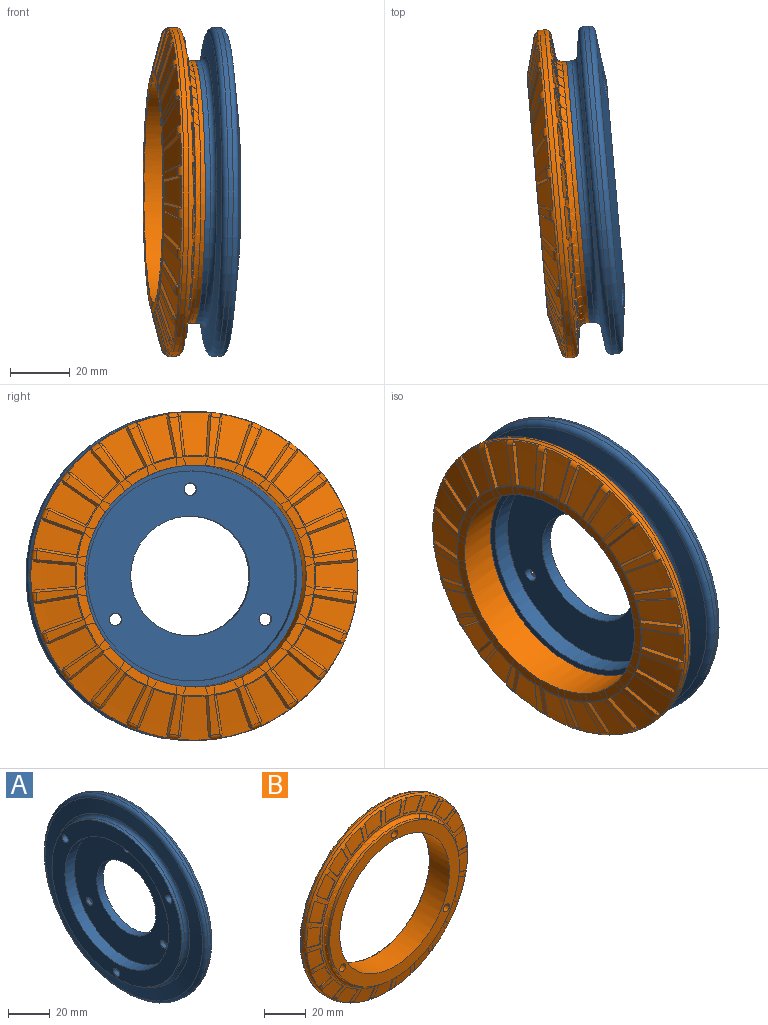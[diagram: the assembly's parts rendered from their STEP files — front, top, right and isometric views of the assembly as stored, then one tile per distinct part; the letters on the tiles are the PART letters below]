
ASSEMBLY  parts=2 mates=1
PART A: 28 faces, bbox 12.7x119.1x119.1 mm
  f0: cone r=53.26mm half-angle=82.5deg, axis (-1,0,0), area 4769.5mm2, adj f1,f12,f21,f24,f27
  f1: torus R=53mm, axis (-1,0,0), area 983.9mm2, adj f0,f2
  f2: cylinder r=55mm len=110mm, axis (-1,0,0), area 573.7mm2, adj f1,f3
  f3: torus R=53mm, axis (-1,0,0), area 983.9mm2, adj f2,f4
  f4: cone r=45.61mm half-angle=82.5deg, axis (1,0,0), area 2395.9mm2, adj f3,f5
  f5: torus R=45.88mm, axis (-1,0,0), area 805.2mm2, adj f4,f6
  f6: cylinder r=43.88mm len=87.75mm, axis (-1,0,0), area 481.3mm2, adj f5,f7
  f7: plane 87.75x87.75mm, normal (-1,0,0), area 2130.1mm2, adj f6,f8,f19,f22,f25
  f8: cylinder r=35.12mm len=70.25mm, axis (-1,0,0), area 1423.4mm2, adj f7,f9
  f9: plane 70.25x70.25mm, normal (-1,0,0), area 2577.8mm2, adj f8,f10,f13,f15,f17
  f10: cylinder r=20mm len=40mm, axis (-1,0,0), area 534.1mm2, adj f9,f11
  f11: plane 71x71mm, normal (1,0,0), area 2551.8mm2, adj f10,f12,f14,f16,f18
  f12: cylinder r=35.5mm len=71mm, axis (-1,0,0), area 446.1mm2, adj f0,f11
  f13: cylinder r=2.1mm len=4.2mm, axis (1,0,0), area 31mm2, adj f9,f14
  f14: cone r=2.1mm half-angle=45deg, axis (1,0,0), area 51.5mm2, adj f11,f13
  f15: cylinder r=2.1mm len=4.2mm, axis (1,0,0), area 31mm2, adj f9,f16
  f16: cone r=2.1mm half-angle=45deg, axis (1,0,0), area 51.5mm2, adj f11,f15
  f17: cylinder r=2.1mm len=4.2mm, axis (1,0,0), area 31mm2, adj f9,f18
  f18: cone r=2.1mm half-angle=45deg, axis (1,0,0), area 51.5mm2, adj f11,f17
  f19: cylinder r=2.1mm len=7.7mm, axis (1,0,0), area 101.6mm2, adj f7,f20
  f20: plane 9.75x9.75mm, normal (1,0,0), area 60.8mm2, adj f19,f21
  f21: cylinder r=4.88mm len=9.75mm, axis (1,0,0), area 132.4mm2, adj f0,f20
  f22: cylinder r=2.1mm len=7.7mm, axis (1,0,0), area 101.6mm2, adj f7,f23
  f23: plane 9.75x9.75mm, normal (1,0,0), area 60.8mm2, adj f22,f24
  f24: cylinder r=4.88mm len=9.75mm, axis (1,0,0), area 132.4mm2, adj f0,f23
  f25: cylinder r=2.1mm len=7.7mm, axis (1,0,0), area 101.6mm2, adj f7,f26
  f26: plane 9.75x9.75mm, normal (1,0,0), area 60.8mm2, adj f25,f27
  f27: cylinder r=4.88mm len=9.75mm, axis (1,0,0), area 132.4mm2, adj f0,f26
PART B: 328 faces, bbox 119.2x14.6x119.2 mm
  f0: revolved ~12.32x11.5mm, area 83mm2, adj f1,f2,f3,f92
  f1: plane 7.92x1.5mm, normal (-0.99,0,-0.16), area 2.9mm2, adj f0,f2,f92,f93
  f2: revolved ~93.19x93.17mm, area 112.1mm2, adj f0,f1,f3,f93
  f3: plane 7.5x2.93mm, normal (0.93,0,0.36), area 2.9mm2, adj f0,f2,f92,f93
  f4: revolved ~13.82x11.86mm, area 83mm2, adj f5,f6,f7,f92
  f5: plane 7.34x3.32mm, normal (-0.91,0,-0.41), area 2.9mm2, adj f4,f6,f92,f93
  f6: revolved ~93.18x93.17mm, area 112.1mm2, adj f4,f5,f7,f93
  f7: plane 6.51x4.75mm, normal (0.81,0,0.59), area 2.9mm2, adj f4,f6,f92,f93
  f8: revolved ~14.37x11.42mm, area 83mm2, adj f9,f10,f11,f92
  f9: plane 6.25x5.08mm, normal (-0.78,0,-0.63), area 2.9mm2, adj f8,f10,f92,f93
  f10: revolved ~8.25x5.29mm, area 3.6mm2, adj f8,f9,f11,f93
  f11: plane 6.25x5.08mm, normal (0.63,0,0.78), area 2.9mm2, adj f8,f10,f92,f93
  f12: revolved ~13.95x10.19mm, area 83mm2, adj f13,f14,f15,f92
  f13: plane 6.51x4.75mm, normal (-0.59,0,-0.81), area 2.9mm2, adj f12,f14,f92,f93
  f14: revolved ~9.32x2.99mm, area 3.6mm2, adj f12,f13,f15,f93
  f15: plane 7.34x3.32mm, normal (0.41,0,0.91), area 2.9mm2, adj f12,f14,f92,f93
  f16: revolved ~12.58x8.3mm, area 83mm2, adj f17,f18,f19,f92
  f17: plane 7.5x2.93mm, normal (-0.36,0,-0.93), area 2.9mm2, adj f16,f18,f92,f93
  f18: revolved ~93.21x93.1mm, area 112.1mm2, adj f16,f17,f19,f93
  f19: plane 7.92x1.5mm, normal (0.16,0,0.99), area 2.9mm2, adj f16,f18,f92,f93
  f20: revolved ~11.18x9.98mm, area 83mm2, adj f21,f22,f23,f92
  f21: plane 7.98x1.5mm, normal (-0.1,0,-0.99), area 2.9mm2, adj f20,f22,f92,f93
  f22: revolved ~9.53x2.14mm, area 3.6mm2, adj f20,f21,f23,f93
  f23: plane 7.98x1.5mm, normal (-0.1,0,0.99), area 2.9mm2, adj f20,f22,f92,f93
  f24: revolved ~12.32x11.5mm, area 83mm2, adj f25,f26,f27,f92
  f25: plane 7.92x1.5mm, normal (0.16,0,-0.99), area 2.9mm2, adj f24,f26,f92,f93
  f26: revolved ~93.19x93.17mm, area 112.1mm2, adj f24,f25,f27,f93
  f27: plane 7.5x2.93mm, normal (-0.36,0,0.93), area 2.9mm2, adj f24,f26,f92,f93
  f28: revolved ~13.82x11.86mm, area 83mm2, adj f29,f30,f31,f92
  f29: plane 7.34x3.32mm, normal (0.41,0,-0.91), area 2.9mm2, adj f28,f30,f92,f93
  f30: revolved ~93.18x93.17mm, area 112.1mm2, adj f28,f29,f31,f93
  f31: plane 6.51x4.75mm, normal (-0.59,0,0.81), area 2.9mm2, adj f28,f30,f92,f93
  f32: revolved ~14.37x11.42mm, area 83mm2, adj f33,f34,f35,f92
  f33: plane 6.25x5.08mm, normal (0.63,0,-0.78), area 2.9mm2, adj f32,f34,f92,f93
  f34: revolved ~8.25x5.29mm, area 3.6mm2, adj f32,f33,f35,f93
  f35: plane 6.25x5.08mm, normal (-0.78,0,0.63), area 2.9mm2, adj f32,f34,f92,f93
  f36: revolved ~13.95x10.19mm, area 83mm2, adj f37,f38,f39,f92
  f37: plane 6.51x4.75mm, normal (0.81,0,-0.59), area 2.9mm2, adj f36,f38,f92,f93
  f38: revolved ~9.32x2.99mm, area 3.6mm2, adj f36,f37,f39,f93
  f39: plane 7.34x3.32mm, normal (-0.91,0,0.41), area 2.9mm2, adj f36,f38,f92,f93
  f40: revolved ~12.58x8.3mm, area 83mm2, adj f41,f42,f43,f92
  f41: plane 7.5x2.93mm, normal (0.93,0,-0.36), area 2.9mm2, adj f40,f42,f92,f93
  f42: revolved ~93.21x93.1mm, area 112.1mm2, adj f40,f41,f43,f93
  f43: plane 7.92x1.5mm, normal (-0.99,0,0.16), area 2.9mm2, adj f40,f42,f92,f93
  f44: revolved ~11.18x9.98mm, area 83mm2, adj f45,f46,f47,f92
  f45: plane 7.98x1.5mm, normal (0.99,0,-0.1), area 2.9mm2, adj f44,f46,f92,f93
  f46: revolved ~9.53x2.14mm, area 3.6mm2, adj f44,f45,f47,f93
  f47: plane 7.98x1.5mm, normal (-0.99,0,-0.1), area 2.9mm2, adj f44,f46,f92,f93
  f48: revolved ~12.32x11.5mm, area 83mm2, adj f49,f50,f51,f92
  f49: plane 7.92x1.5mm, normal (0.99,0,0.16), area 2.9mm2, adj f48,f50,f92,f93
  f50: revolved ~93.19x93.17mm, area 112.1mm2, adj f48,f49,f51,f93
  f51: plane 7.5x2.93mm, normal (-0.93,0,-0.36), area 2.9mm2, adj f48,f50,f92,f93
  f52: revolved ~13.82x11.86mm, area 83mm2, adj f53,f54,f55,f92
  f53: plane 7.34x3.32mm, normal (0.91,0,0.41), area 2.9mm2, adj f52,f54,f92,f93
  f54: revolved ~93.18x93.17mm, area 112.1mm2, adj f52,f53,f55,f93
  f55: plane 6.51x4.75mm, normal (-0.81,0,-0.59), area 2.9mm2, adj f52,f54,f92,f93
  f56: revolved ~14.37x11.42mm, area 83mm2, adj f57,f58,f59,f92
  f57: plane 6.25x5.08mm, normal (0.78,0,0.63), area 2.9mm2, adj f56,f58,f92,f93
  f58: revolved ~8.25x5.29mm, area 3.6mm2, adj f56,f57,f59,f93
  f59: plane 6.25x5.08mm, normal (-0.63,0,-0.78), area 2.9mm2, adj f56,f58,f92,f93
  f60: revolved ~13.95x10.19mm, area 83mm2, adj f61,f62,f63,f92
  f61: plane 6.51x4.75mm, normal (0.59,0,0.81), area 2.9mm2, adj f60,f62,f92,f93
  f62: revolved ~9.32x2.99mm, area 3.6mm2, adj f60,f61,f63,f93
  f63: plane 7.34x3.32mm, normal (-0.41,0,-0.91), area 2.9mm2, adj f60,f62,f92,f93
  f64: revolved ~12.58x8.3mm, area 83mm2, adj f65,f66,f67,f92
  f65: plane 7.5x2.93mm, normal (0.36,0,0.93), area 2.9mm2, adj f64,f66,f92,f93
  f66: revolved ~93.21x93.1mm, area 112.1mm2, adj f64,f65,f67,f93
  f67: plane 7.92x1.5mm, normal (-0.16,0,-0.99), area 2.9mm2, adj f64,f66,f92,f93
  f68: revolved ~11.18x9.98mm, area 83mm2, adj f69,f70,f71,f92
  f69: plane 7.98x1.5mm, normal (0.1,0,0.99), area 2.9mm2, adj f68,f70,f92,f93
  f70: revolved ~9.53x2.14mm, area 3.6mm2, adj f68,f69,f71,f93
  f71: plane 7.98x1.5mm, normal (0.1,0,-0.99), area 2.9mm2, adj f68,f70,f92,f93
  f72: revolved ~12.32x11.5mm, area 83mm2, adj f73,f74,f75,f92
  f73: plane 7.92x1.5mm, normal (-0.16,0,0.99), area 2.9mm2, adj f72,f74,f92,f93
  f74: revolved ~93.19x93.17mm, area 112.1mm2, adj f72,f73,f75,f93
  f75: plane 7.5x2.93mm, normal (0.36,0,-0.93), area 2.9mm2, adj f72,f74,f92,f93
  f76: revolved ~13.82x11.86mm, area 83mm2, adj f77,f78,f79,f92
  f77: plane 7.34x3.32mm, normal (-0.41,0,0.91), area 2.9mm2, adj f76,f78,f92,f93
  f78: revolved ~93.18x93.17mm, area 112.1mm2, adj f76,f77,f79,f93
  f79: plane 6.51x4.75mm, normal (0.59,0,-0.81), area 2.9mm2, adj f76,f78,f92,f93
  f80: revolved ~14.37x11.42mm, area 83mm2, adj f81,f82,f83,f92
  f81: plane 6.25x5.08mm, normal (-0.63,0,0.78), area 2.9mm2, adj f80,f82,f92,f93
  f82: revolved ~8.25x5.29mm, area 3.6mm2, adj f80,f81,f83,f93
  f83: plane 6.25x5.08mm, normal (0.78,0,-0.63), area 2.9mm2, adj f80,f82,f92,f93
  f84: revolved ~13.95x10.19mm, area 83mm2, adj f85,f86,f87,f92
  f85: plane 6.51x4.75mm, normal (-0.81,0,0.59), area 2.9mm2, adj f84,f86,f92,f93
  f86: revolved ~9.32x2.99mm, area 3.6mm2, adj f84,f85,f87,f93
  f87: plane 7.34x3.32mm, normal (0.91,0,-0.41), area 2.9mm2, adj f84,f86,f92,f93
  f88: revolved ~12.58x8.3mm, area 83mm2, adj f89,f90,f91,f92
  f89: plane 7.5x2.93mm, normal (-0.93,0,0.36), area 2.9mm2, adj f88,f90,f92,f93
  f90: revolved ~93.21x93.1mm, area 112.1mm2, adj f88,f89,f91,f93
  f91: plane 7.92x1.5mm, normal (0.99,0,-0.16), area 2.9mm2, adj f88,f90,f92,f93
  f92: torus R=53mm, axis (0,-1,0), area 639.7mm2, adj f0,f1,f3,f4,f5,f7,f8,f9
  f93: cone r=45.61mm half-angle=82.5deg, axis (0,1,0), area 724.2mm2, adj f1,f2,f3,f5,f6,f7,f9,f10
  f94: bspline ~15.1x6.29mm, area 17.1mm2, adj f95,f98,f99,f100,f101,f307
  f95: bspline ~1.52x1.3mm, area 0.9mm2, adj f94,f99,f308
  f96: bspline ~16.08x5.05mm, area 17.1mm2, adj f97,f98,f99,f101,f102,f307
  f97: bspline ~1.69x1.52mm, area 0.9mm2, adj f96,f99,f308
  f98: cone r=56.02mm half-angle=89.5deg, axis (0,1,0), area 0.3mm2, adj f94,f96,f101,f307
  f99: cone r=56.07mm half-angle=75.5deg, axis (0,-1,0), area 148.4mm2, adj f94,f95,f96,f97,f100,f102,f305,f308
  f100: plane 13.71x4.99mm, normal (0.94,0,0.34), area 0.9mm2, adj f94,f99,f101,f305
  f101: plane 8.33x5.04mm, normal (0,-1,0), area 24.7mm2, adj f94,f96,f98,f100,f102,f305
  f102: plane 14.37x3.85mm, normal (-0.98,0,-0.17), area 0.9mm2, adj f96,f99,f101,f305
  f103: bspline ~13.38x9.94mm, area 17.1mm2, adj f104,f107,f108,f109,f110,f307
  f104: bspline ~1.56x1.52mm, area 0.9mm2, adj f103,f108,f308
  f105: bspline ~15.01x7.4mm, area 17.1mm2, adj f106,f107,f108,f110,f111,f307
  f106: bspline ~1.76x1.52mm, area 0.9mm2, adj f105,f108,f308
  f107: cone r=56.02mm half-angle=89.5deg, axis (0,1,0), area 0.3mm2, adj f103,f105,f110,f307
  f108: cone r=56.07mm half-angle=75.5deg, axis (0,-1,0), area 148.4mm2, adj f103,f104,f105,f106,f109,f111,f305,f308
  f109: plane 11.95x8.37mm, normal (0.82,0,0.57), area 0.9mm2, adj f103,f108,f110,f305
  f110: plane 8.13x6.54mm, normal (0,-1,0), area 24.7mm2, adj f103,f105,f107,f109,f111,f305
  f111: plane 13.23x6.17mm, normal (-0.91,0,-0.42), area 0.9mm2, adj f105,f108,f110,f305
  f112: bspline ~12.92x10.76mm, area 17.1mm2, adj f113,f116,f117,f118,f119,f307
  f113: bspline ~1.72x1.52mm, area 0.9mm2, adj f112,f117,f308
  f114: bspline ~12.92x10.76mm, area 17.1mm2, adj f115,f116,f117,f119,f120,f307
  f115: bspline ~1.72x1.52mm, area 0.9mm2, adj f114,f117,f308
  f116: cone r=56.02mm half-angle=89.5deg, axis (0,1,0), area 0.3mm2, adj f112,f114,f119,f307
  f117: cone r=56.07mm half-angle=75.5deg, axis (0,-1,0), area 148.4mm2, adj f112,f113,f114,f115,f118,f120,f305,f308
  f118: plane 11.18x9.38mm, normal (0.64,0,0.77), area 0.9mm2, adj f112,f117,f119,f305
  f119: plane 7.6x7.6mm, normal (0,-1,0), area 24.7mm2, adj f112,f114,f116,f118,f120,f305
  f120: plane 11.18x9.38mm, normal (-0.77,0,-0.64), area 0.9mm2, adj f114,f117,f119,f305
  f121: bspline ~15.01x7.4mm, area 17.1mm2, adj f122,f125,f126,f127,f128,f307
  f122: bspline ~1.76x1.52mm, area 0.9mm2, adj f121,f126,f308
  f123: bspline ~13.38x9.94mm, area 17.1mm2, adj f124,f125,f126,f128,f129,f307
  f124: bspline ~1.56x1.52mm, area 0.9mm2, adj f123,f126,f308
  f125: cone r=56.02mm half-angle=89.5deg, axis (0,1,0), area 0.3mm2, adj f121,f123,f128,f307
  f126: cone r=56.07mm half-angle=75.5deg, axis (0,-1,0), area 148.4mm2, adj f121,f122,f123,f124,f127,f129,f305,f308
  f127: plane 13.23x6.17mm, normal (0.42,0,0.91), area 0.9mm2, adj f121,f126,f128,f305
  f128: plane 8.13x6.54mm, normal (0,-1,0), area 24.7mm2, adj f121,f123,f125,f127,f129,f305
  f129: plane 11.95x8.37mm, normal (-0.57,0,-0.82), area 0.9mm2, adj f123,f126,f128,f305
  f130: bspline ~16.08x5.05mm, area 17.1mm2, adj f131,f134,f135,f136,f137,f307
  f131: bspline ~1.69x1.52mm, area 0.9mm2, adj f130,f135,f308
  f132: bspline ~15.1x6.29mm, area 17.1mm2, adj f133,f134,f135,f137,f138,f307
  f133: bspline ~1.52x1.3mm, area 0.9mm2, adj f132,f135,f308
  f134: cone r=56.02mm half-angle=89.5deg, axis (0,1,0), area 0.3mm2, adj f130,f132,f137,f307
  f135: cone r=56.07mm half-angle=75.5deg, axis (0,-1,0), area 148.4mm2, adj f130,f131,f132,f133,f136,f138,f305,f308
  f136: plane 14.37x3.85mm, normal (0.17,0,0.98), area 0.9mm2, adj f130,f135,f137,f305
  f137: plane 8.33x5.04mm, normal (0,-1,0), area 24.7mm2, adj f130,f132,f134,f136,f138,f305
  f138: plane 13.71x4.99mm, normal (-0.34,0,-0.94), area 0.9mm2, adj f132,f135,f137,f305
  f139: bspline ~16.85x5.27mm, area 17.1mm2, adj f140,f143,f144,f145,f146,f307
  f140: bspline ~1.52x1.49mm, area 0.9mm2, adj f139,f144,f308
  f141: bspline ~16.85x5.27mm, area 17.1mm2, adj f142,f143,f144,f146,f147,f307
  f142: bspline ~1.52x1.49mm, area 0.9mm2, adj f141,f144,f308
  f143: cone r=56.02mm half-angle=89.5deg, axis (0,1,0), area 0.3mm2, adj f139,f141,f146,f307
  f144: cone r=56.07mm half-angle=75.5deg, axis (0,-1,0), area 148.4mm2, adj f139,f140,f141,f142,f145,f147,f305,f308
  f145: plane 14.54x3.85mm, normal (-0.09,0,1), area 0.9mm2, adj f139,f144,f146,f305
  f146: plane 8.62x3.43mm, normal (0,-1,0), area 24.7mm2, adj f139,f141,f143,f145,f147,f305
  f147: plane 14.54x3.85mm, normal (-0.09,0,-1), area 0.9mm2, adj f141,f144,f146,f305
  f148: bspline ~15.1x6.29mm, area 17.1mm2, adj f149,f152,f153,f154,f155,f307
  f149: bspline ~1.52x1.3mm, area 0.9mm2, adj f148,f153,f308
  f150: bspline ~16.08x5.05mm, area 17.1mm2, adj f151,f152,f153,f155,f156,f307
  f151: bspline ~1.69x1.52mm, area 0.9mm2, adj f150,f153,f308
  f152: cone r=56.02mm half-angle=89.5deg, axis (0,1,0), area 0.3mm2, adj f148,f150,f155,f307
  f153: cone r=56.07mm half-angle=75.5deg, axis (0,-1,0), area 148.4mm2, adj f148,f149,f150,f151,f154,f156,f305,f308
  f154: plane 13.71x4.99mm, normal (-0.34,0,0.94), area 0.9mm2, adj f148,f153,f155,f305
  f155: plane 8.33x5.04mm, normal (0,-1,0), area 24.7mm2, adj f148,f150,f152,f154,f156,f305
  f156: plane 14.37x3.85mm, normal (0.17,0,-0.98), area 0.9mm2, adj f150,f153,f155,f305
  f157: bspline ~13.38x9.94mm, area 17.1mm2, adj f158,f161,f162,f163,f164,f307
  f158: bspline ~1.56x1.52mm, area 0.9mm2, adj f157,f162,f308
  f159: bspline ~15.01x7.4mm, area 17.1mm2, adj f160,f161,f162,f164,f165,f307
  f160: bspline ~1.76x1.52mm, area 0.9mm2, adj f159,f162,f308
  f161: cone r=56.02mm half-angle=89.5deg, axis (0,1,0), area 0.3mm2, adj f157,f159,f164,f307
  f162: cone r=56.07mm half-angle=75.5deg, axis (0,-1,0), area 148.4mm2, adj f157,f158,f159,f160,f163,f165,f305,f308
  f163: plane 11.95x8.37mm, normal (-0.57,0,0.82), area 0.9mm2, adj f157,f162,f164,f305
  f164: plane 8.13x6.54mm, normal (0,-1,0), area 24.7mm2, adj f157,f159,f161,f163,f165,f305
  f165: plane 13.23x6.17mm, normal (0.42,0,-0.91), area 0.9mm2, adj f159,f162,f164,f305
  f166: bspline ~12.92x10.76mm, area 17.1mm2, adj f167,f170,f171,f172,f173,f307
  f167: bspline ~1.72x1.52mm, area 0.9mm2, adj f166,f171,f308
  f168: bspline ~12.92x10.76mm, area 17.1mm2, adj f169,f170,f171,f173,f174,f307
  f169: bspline ~1.72x1.52mm, area 0.9mm2, adj f168,f171,f308
  f170: cone r=56.02mm half-angle=89.5deg, axis (0,1,0), area 0.3mm2, adj f166,f168,f173,f307
  f171: cone r=56.07mm half-angle=75.5deg, axis (0,-1,0), area 148.4mm2, adj f166,f167,f168,f169,f172,f174,f305,f308
  f172: plane 11.18x9.38mm, normal (-0.77,0,0.64), area 0.9mm2, adj f166,f171,f173,f305
  f173: plane 7.6x7.6mm, normal (0,-1,0), area 24.7mm2, adj f166,f168,f170,f172,f174,f305
  f174: plane 11.18x9.38mm, normal (0.64,0,-0.77), area 0.9mm2, adj f168,f171,f173,f305
  f175: bspline ~15.01x7.4mm, area 17.1mm2, adj f176,f179,f180,f181,f182,f307
  f176: bspline ~1.76x1.52mm, area 0.9mm2, adj f175,f180,f308
  f177: bspline ~13.38x9.94mm, area 17.1mm2, adj f178,f179,f180,f182,f183,f307
  f178: bspline ~1.56x1.52mm, area 0.9mm2, adj f177,f180,f308
  f179: cone r=56.02mm half-angle=89.5deg, axis (0,1,0), area 0.3mm2, adj f175,f177,f182,f307
  f180: cone r=56.07mm half-angle=75.5deg, axis (0,-1,0), area 148.4mm2, adj f175,f176,f177,f178,f181,f183,f305,f308
  f181: plane 13.23x6.17mm, normal (-0.91,0,0.42), area 0.9mm2, adj f175,f180,f182,f305
  f182: plane 8.13x6.54mm, normal (0,-1,0), area 24.7mm2, adj f175,f177,f179,f181,f183,f305
  f183: plane 11.95x8.37mm, normal (0.82,0,-0.57), area 0.9mm2, adj f177,f180,f182,f305
  f184: bspline ~16.08x5.05mm, area 17.1mm2, adj f185,f188,f189,f190,f191,f307
  f185: bspline ~1.69x1.52mm, area 0.9mm2, adj f184,f189,f308
  f186: bspline ~15.1x6.29mm, area 17.1mm2, adj f187,f188,f189,f191,f192,f307
  f187: bspline ~1.52x1.3mm, area 0.9mm2, adj f186,f189,f308
  f188: cone r=56.02mm half-angle=89.5deg, axis (0,1,0), area 0.3mm2, adj f184,f186,f191,f307
  f189: cone r=56.07mm half-angle=75.5deg, axis (0,-1,0), area 148.4mm2, adj f184,f185,f186,f187,f190,f192,f305,f308
  f190: plane 14.37x3.85mm, normal (-0.98,0,0.17), area 0.9mm2, adj f184,f189,f191,f305
  f191: plane 8.33x5.04mm, normal (0,-1,0), area 24.7mm2, adj f184,f186,f188,f190,f192,f305
  f192: plane 13.71x4.99mm, normal (0.94,0,-0.34), area 0.9mm2, adj f186,f189,f191,f305
  f193: bspline ~16.85x5.27mm, area 17.1mm2, adj f194,f197,f198,f199,f200,f307
  f194: bspline ~1.52x1.49mm, area 0.9mm2, adj f193,f198,f308
  f195: bspline ~16.85x5.27mm, area 17.1mm2, adj f196,f197,f198,f200,f201,f307
  f196: bspline ~1.52x1.49mm, area 0.9mm2, adj f195,f198,f308
  f197: cone r=56.02mm half-angle=89.5deg, axis (0,1,0), area 0.3mm2, adj f193,f195,f200,f307
  f198: cone r=56.07mm half-angle=75.5deg, axis (0,-1,0), area 148.4mm2, adj f193,f194,f195,f196,f199,f201,f305,f308
  f199: plane 14.54x3.85mm, normal (-1,0,-0.09), area 0.9mm2, adj f193,f198,f200,f305
  f200: plane 8.62x3.43mm, normal (0,-1,0), area 24.7mm2, adj f193,f195,f197,f199,f201,f305
  f201: plane 14.54x3.85mm, normal (1,0,-0.09), area 0.9mm2, adj f195,f198,f200,f305
  f202: bspline ~15.1x6.29mm, area 17.1mm2, adj f203,f206,f207,f208,f209,f307
  f203: bspline ~1.52x1.3mm, area 0.9mm2, adj f202,f207,f308
  f204: bspline ~16.08x5.05mm, area 17.1mm2, adj f205,f206,f207,f209,f210,f307
  f205: bspline ~1.69x1.52mm, area 0.9mm2, adj f204,f207,f308
  f206: cone r=56.02mm half-angle=89.5deg, axis (0,1,0), area 0.3mm2, adj f202,f204,f209,f307
  f207: cone r=56.07mm half-angle=75.5deg, axis (0,-1,0), area 148.4mm2, adj f202,f203,f204,f205,f208,f210,f305,f308
  f208: plane 13.71x4.99mm, normal (-0.94,0,-0.34), area 0.9mm2, adj f202,f207,f209,f305
  f209: plane 8.33x5.04mm, normal (0,-1,0), area 24.7mm2, adj f202,f204,f206,f208,f210,f305
  f210: plane 14.37x3.85mm, normal (0.98,0,0.17), area 0.9mm2, adj f204,f207,f209,f305
  f211: bspline ~13.38x9.94mm, area 17.1mm2, adj f212,f215,f216,f217,f218,f307
  f212: bspline ~1.56x1.52mm, area 0.9mm2, adj f211,f216,f308
  f213: bspline ~15.01x7.4mm, area 17.1mm2, adj f214,f215,f216,f218,f219,f307
  f214: bspline ~1.76x1.52mm, area 0.9mm2, adj f213,f216,f308
  f215: cone r=56.02mm half-angle=89.5deg, axis (0,1,0), area 0.3mm2, adj f211,f213,f218,f307
  f216: cone r=56.07mm half-angle=75.5deg, axis (0,-1,0), area 148.4mm2, adj f211,f212,f213,f214,f217,f219,f305,f308
  f217: plane 11.95x8.37mm, normal (-0.82,0,-0.57), area 0.9mm2, adj f211,f216,f218,f305
  f218: plane 8.13x6.54mm, normal (0,-1,0), area 24.7mm2, adj f211,f213,f215,f217,f219,f305
  f219: plane 13.23x6.17mm, normal (0.91,0,0.42), area 0.9mm2, adj f213,f216,f218,f305
  f220: bspline ~12.92x10.76mm, area 17.1mm2, adj f221,f224,f225,f226,f227,f307
  f221: bspline ~1.72x1.52mm, area 0.9mm2, adj f220,f225,f308
  f222: bspline ~12.92x10.76mm, area 17.1mm2, adj f223,f224,f225,f227,f228,f307
  f223: bspline ~1.72x1.52mm, area 0.9mm2, adj f222,f225,f308
  f224: cone r=56.02mm half-angle=89.5deg, axis (0,1,0), area 0.3mm2, adj f220,f222,f227,f307
  f225: cone r=56.07mm half-angle=75.5deg, axis (0,-1,0), area 148.4mm2, adj f220,f221,f222,f223,f226,f228,f305,f308
  f226: plane 11.18x9.38mm, normal (-0.64,0,-0.77), area 0.9mm2, adj f220,f225,f227,f305
  f227: plane 7.6x7.6mm, normal (0,-1,0), area 24.7mm2, adj f220,f222,f224,f226,f228,f305
  f228: plane 11.18x9.38mm, normal (0.77,0,0.64), area 0.9mm2, adj f222,f225,f227,f305
  f229: bspline ~15.01x7.4mm, area 17.1mm2, adj f230,f233,f234,f235,f236,f307
  f230: bspline ~1.76x1.52mm, area 0.9mm2, adj f229,f234,f308
  f231: bspline ~13.38x9.94mm, area 17.1mm2, adj f232,f233,f234,f236,f237,f307
  f232: bspline ~1.56x1.52mm, area 0.9mm2, adj f231,f234,f308
  f233: cone r=56.02mm half-angle=89.5deg, axis (0,1,0), area 0.3mm2, adj f229,f231,f236,f307
  f234: cone r=56.07mm half-angle=75.5deg, axis (0,-1,0), area 148.4mm2, adj f229,f230,f231,f232,f235,f237,f305,f308
  f235: plane 13.23x6.17mm, normal (-0.42,0,-0.91), area 0.9mm2, adj f229,f234,f236,f305
  f236: plane 8.13x6.54mm, normal (0,-1,0), area 24.7mm2, adj f229,f231,f233,f235,f237,f305
  f237: plane 11.95x8.37mm, normal (0.57,0,0.82), area 0.9mm2, adj f231,f234,f236,f305
  f238: bspline ~16.08x5.05mm, area 17.1mm2, adj f239,f242,f243,f244,f245,f307
  f239: bspline ~1.69x1.52mm, area 0.9mm2, adj f238,f243,f308
  f240: bspline ~15.1x6.29mm, area 17.1mm2, adj f241,f242,f243,f245,f246,f307
  f241: bspline ~1.52x1.3mm, area 0.9mm2, adj f240,f243,f308
  f242: cone r=56.02mm half-angle=89.5deg, axis (0,1,0), area 0.3mm2, adj f238,f240,f245,f307
  f243: cone r=56.07mm half-angle=75.5deg, axis (0,-1,0), area 148.4mm2, adj f238,f239,f240,f241,f244,f246,f305,f308
  f244: plane 14.37x3.85mm, normal (-0.17,0,-0.98), area 0.9mm2, adj f238,f243,f245,f305
  f245: plane 8.33x5.04mm, normal (0,-1,0), area 24.7mm2, adj f238,f240,f242,f244,f246,f305
  f246: plane 13.71x4.99mm, normal (0.34,0,0.94), area 0.9mm2, adj f240,f243,f245,f305
  f247: bspline ~16.85x5.27mm, area 17.1mm2, adj f248,f251,f252,f253,f254,f307
  f248: bspline ~1.52x1.49mm, area 0.9mm2, adj f247,f252,f308
  f249: bspline ~16.85x5.27mm, area 17.1mm2, adj f250,f251,f252,f254,f255,f307
  f250: bspline ~1.52x1.49mm, area 0.9mm2, adj f249,f252,f308
  f251: cone r=56.02mm half-angle=89.5deg, axis (0,1,0), area 0.3mm2, adj f247,f249,f254,f307
  f252: cone r=56.07mm half-angle=75.5deg, axis (0,-1,0), area 148.4mm2, adj f247,f248,f249,f250,f253,f255,f305,f308
  f253: plane 14.54x3.85mm, normal (0.09,0,-1), area 0.9mm2, adj f247,f252,f254,f305
  f254: plane 8.62x3.43mm, normal (0,-1,0), area 24.7mm2, adj f247,f249,f251,f253,f255,f305
  f255: plane 14.54x3.85mm, normal (0.09,0,1), area 0.9mm2, adj f249,f252,f254,f305
  f256: bspline ~15.1x6.29mm, area 17.1mm2, adj f257,f260,f261,f262,f263,f307
  f257: bspline ~1.52x1.3mm, area 0.9mm2, adj f256,f261,f308
  f258: bspline ~16.08x5.05mm, area 17.1mm2, adj f259,f260,f261,f263,f264,f307
  f259: bspline ~1.69x1.52mm, area 0.9mm2, adj f258,f261,f308
  f260: cone r=56.02mm half-angle=89.5deg, axis (0,1,0), area 0.3mm2, adj f256,f258,f263,f307
  f261: cone r=56.07mm half-angle=75.5deg, axis (0,-1,0), area 148.4mm2, adj f256,f257,f258,f259,f262,f264,f305,f308
  f262: plane 13.71x4.99mm, normal (0.34,0,-0.94), area 0.9mm2, adj f256,f261,f263,f305
  f263: plane 8.33x5.04mm, normal (0,-1,0), area 24.7mm2, adj f256,f258,f260,f262,f264,f305
  f264: plane 14.37x3.85mm, normal (-0.17,0,0.98), area 0.9mm2, adj f258,f261,f263,f305
  f265: bspline ~13.38x9.94mm, area 17.1mm2, adj f266,f269,f270,f271,f272,f307
  f266: bspline ~1.56x1.52mm, area 0.9mm2, adj f265,f270,f308
  f267: bspline ~15.01x7.4mm, area 17.1mm2, adj f268,f269,f270,f272,f273,f307
  f268: bspline ~1.76x1.52mm, area 0.9mm2, adj f267,f270,f308
  f269: cone r=56.02mm half-angle=89.5deg, axis (0,1,0), area 0.3mm2, adj f265,f267,f272,f307
  f270: cone r=56.07mm half-angle=75.5deg, axis (0,-1,0), area 148.4mm2, adj f265,f266,f267,f268,f271,f273,f305,f308
  f271: plane 11.95x8.37mm, normal (0.57,0,-0.82), area 0.9mm2, adj f265,f270,f272,f305
  f272: plane 8.13x6.54mm, normal (0,-1,0), area 24.7mm2, adj f265,f267,f269,f271,f273,f305
  f273: plane 13.23x6.17mm, normal (-0.42,0,0.91), area 0.9mm2, adj f267,f270,f272,f305
  f274: bspline ~12.92x10.76mm, area 17.1mm2, adj f275,f278,f279,f280,f281,f307
  f275: bspline ~1.72x1.52mm, area 0.9mm2, adj f274,f279,f308
  f276: bspline ~12.92x10.76mm, area 17.1mm2, adj f277,f278,f279,f281,f282,f307
  f277: bspline ~1.72x1.52mm, area 0.9mm2, adj f276,f279,f308
  f278: cone r=56.02mm half-angle=89.5deg, axis (0,1,0), area 0.3mm2, adj f274,f276,f281,f307
  f279: cone r=56.07mm half-angle=75.5deg, axis (0,-1,0), area 148.4mm2, adj f274,f275,f276,f277,f280,f282,f305,f308
  f280: plane 11.18x9.38mm, normal (0.77,0,-0.64), area 0.9mm2, adj f274,f279,f281,f305
  f281: plane 7.6x7.6mm, normal (0,-1,0), area 24.7mm2, adj f274,f276,f278,f280,f282,f305
  f282: plane 11.18x9.38mm, normal (-0.64,0,0.77), area 0.9mm2, adj f276,f279,f281,f305
  f283: bspline ~15.01x7.4mm, area 17.1mm2, adj f284,f287,f288,f289,f290,f307
  f284: bspline ~1.76x1.52mm, area 0.9mm2, adj f283,f288,f308
  f285: bspline ~13.38x9.94mm, area 17.1mm2, adj f286,f287,f288,f290,f291,f307
  f286: bspline ~1.56x1.52mm, area 0.9mm2, adj f285,f288,f308
  f287: cone r=56.02mm half-angle=89.5deg, axis (0,1,0), area 0.3mm2, adj f283,f285,f290,f307
  f288: cone r=56.07mm half-angle=75.5deg, axis (0,-1,0), area 148.4mm2, adj f283,f284,f285,f286,f289,f291,f305,f308
  f289: plane 13.23x6.17mm, normal (0.91,0,-0.42), area 0.9mm2, adj f283,f288,f290,f305
  f290: plane 8.13x6.54mm, normal (0,-1,0), area 24.7mm2, adj f283,f285,f287,f289,f291,f305
  f291: plane 11.95x8.37mm, normal (-0.82,0,0.57), area 0.9mm2, adj f285,f288,f290,f305
  f292: bspline ~16.08x5.05mm, area 17.1mm2, adj f293,f296,f297,f298,f299,f307
  f293: bspline ~1.69x1.52mm, area 0.9mm2, adj f292,f297,f308
  f294: bspline ~15.1x6.29mm, area 17.1mm2, adj f295,f296,f297,f299,f300,f307
  f295: bspline ~1.52x1.3mm, area 0.9mm2, adj f294,f297,f308
  f296: cone r=56.02mm half-angle=89.5deg, axis (0,1,0), area 0.3mm2, adj f292,f294,f299,f307
  f297: cone r=56.07mm half-angle=75.5deg, axis (0,-1,0), area 148.4mm2, adj f292,f293,f294,f295,f298,f300,f305,f308
  f298: plane 14.37x3.85mm, normal (0.98,0,-0.17), area 0.9mm2, adj f292,f297,f299,f305
  f299: plane 8.33x5.04mm, normal (0,-1,0), area 24.7mm2, adj f292,f294,f296,f298,f300,f305
  f300: plane 13.71x4.99mm, normal (-0.94,0,0.34), area 0.9mm2, adj f294,f297,f299,f305
  f301: cylinder r=55mm len=110mm, axis (0,-1,0), area 573.7mm2, adj f92,f308
  f302: torus R=45.88mm, axis (0,-1,0), area 805.2mm2, adj f93,f303
  f303: cylinder r=43.88mm len=87.75mm, axis (0,-1,0), area 405.8mm2, adj f302,f304
  f304: plane 87.75x87.75mm, normal (0,-1,0), area 1681.9mm2, adj f303,f305,f310,f312,f314
  f305: cylinder r=37.1mm len=74.2mm, axis (0,-1,0), area 3167.6mm2, adj f99,f100,f101,f102,f108,f109,f110,f111
  f306: plane 80.2x80.2mm, normal (0,1,0), area 727.6mm2, adj f305,f307
  f307: cone r=53.52mm half-angle=75deg, axis (0,-1,0), area 894.8mm2, adj f94,f96,f98,f103,f105,f107,f112,f114
  f308: torus R=53mm, axis (0,-1,0), area 410.7mm2, adj f95,f97,f99,f104,f106,f108,f113,f115
  f309: cone r=0mm half-angle=59deg, axis (0,-1,0), area 16.2mm2, adj f310
  f310: cylinder r=2.1mm len=8mm, axis (0,-1,0), area 105.6mm2, adj f304,f309
  f311: cone r=0mm half-angle=59deg, axis (0,-1,0), area 16.2mm2, adj f312
  f312: cylinder r=2.1mm len=8mm, axis (0,-1,0), area 105.6mm2, adj f304,f311
  f313: cone r=0mm half-angle=59deg, axis (0,-1,0), area 16.2mm2, adj f314
  f314: cylinder r=2.1mm len=8mm, axis (0,-1,0), area 105.6mm2, adj f304,f313
  f315: plane 8.62x3.43mm, normal (0,-1,0), area 24.7mm2, adj f305,f317,f318,f319,f320,f322
  f316: cone r=56.07mm half-angle=75.5deg, axis (0,-1,0), area 148.4mm2, adj f305,f308,f317,f318,f320,f321,f322,f323
  f317: plane 14.54x3.85mm, normal (-1,0,0.09), area 0.9mm2, adj f305,f315,f316,f320
  f318: plane 14.54x3.85mm, normal (1,0,0.09), area 0.9mm2, adj f305,f315,f316,f322
  f319: cone r=56.02mm half-angle=89.5deg, axis (0,1,0), area 0.3mm2, adj f307,f315,f320,f322
  f320: bspline ~16.85x5.27mm, area 17.1mm2, adj f307,f315,f316,f317,f319,f321
  f321: bspline ~1.52x1.49mm, area 0.9mm2, adj f308,f316,f320
  f322: bspline ~16.85x5.27mm, area 17.1mm2, adj f307,f315,f316,f318,f319,f323
  f323: bspline ~1.52x1.49mm, area 0.9mm2, adj f308,f316,f322
  f324: revolved ~11.18x9.98mm, area 83mm2, adj f92,f325,f326,f327
  f325: plane 7.98x1.5mm, normal (0.99,0,0.1), area 2.9mm2, adj f92,f93,f324,f327
  f326: plane 7.98x1.5mm, normal (-0.99,0,0.1), area 2.9mm2, adj f92,f93,f324,f327
  f327: revolved ~9.53x2.14mm, area 3.6mm2, adj f93,f324,f325,f326
PLACE A rot(axis=(0,0,1),4.9deg) t=(-65.15,-20.28,20.08)mm
PLACE B rot(axis=(0,0,1),94.9deg) t=(-70.8,-20.77,20.08)mm
MATE planar A.f0 <-> B.f92  axis (-1,-0.09,0) through (-65.15,-20.28,20.08)mm
